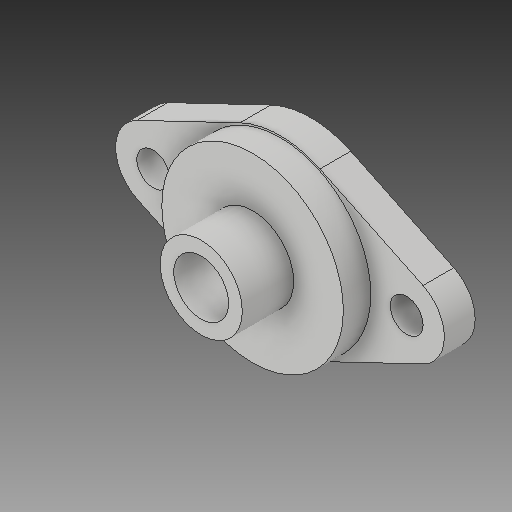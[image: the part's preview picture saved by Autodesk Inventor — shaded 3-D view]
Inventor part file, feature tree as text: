
AUTODESK INVENTOR PART (.ipt)
format: ipt  version: 2017 (Build 210142000, 142)  size: 171,008 bytes
history: native  units: mm
features: extrude x3, sketch x2, other x1, mirror x1
ambient origin geometry x8: Origin, YZ Plane, XZ Plane, XY Plane, X Axis, Y Axis, Z Axis, Center Point
bodies: Body1 (feature_tree)
feature tree (7):
  other  "Твердое тело1"
  extrude  "Выдавливание1"  Depth=8.0mm
  mirror  "Зеркальное отражение1"
  extrude  "Выдавливание2"  Depth=27.0mm
  extrude  "Выдавливание5"  Depth=37.0mm
  sketch  "Эскиз2"
  sketch  "Эскиз5"
